FCSTD DOCUMENT  (FreeCAD 0.21R33771 (Git))
Label: bridge
License: All rights reserved
objects: Part::FeaturePython×22, Part::Mirroring×11, Part::MultiFuse×7, App::FeaturePython×7, Sketcher::SketchObject×5, Part::Extrusion×4, Part::Sweep×3, App::Part×3, Part::Compound×2, Part::Loft×1, Spreadsheet::Sheet×1
note: 54 computed .brp shape members not serialized (recipe doc carries the construction recipe); baked Part::Feature solids carry a one-line shape summary decoded from their .brp

FEATURE [Sketcher::SketchObject] Sketch
  FullyConstrained = true
  sketch-geometry (5):
    g0: LineSegment StartX=-680 StartY=-750 StartZ=0 EndX=-680 EndY=750 EndZ=0
    g1: LineSegment StartX=-680 StartY=750 StartZ=0 EndX=680 EndY=750 EndZ=0
    g2: LineSegment StartX=680 StartY=750 StartZ=0 EndX=680 EndY=-750 EndZ=0
    g3: LineSegment StartX=680 StartY=-750 StartZ=0 EndX=-680 EndY=-750 EndZ=0
    g4: GeomPoint X=0 Y=0 Z=0
  constraints (12):
    c: Coincident(g0,g1)
    c: Coincident(g1,g2)
    c: Coincident(g2,g3)
    c: Coincident(g3,g0)
    c: Horizontal(g1)
    c: Horizontal(g3)
    c: Vertical(g0)
    c: Vertical(g2)
    c: Symmetric(g1,g0,g4)
    c: Coincident(g4,g-1)
    c: DistanceY(g2,g2) = 1500
    c: DistanceX(g1,g1) = 1360
FEATURE [Part::FeaturePython] HShapeSteel  # WARN: FeaturePython — macro-defined, semantics opaque (R4)
  B = 150
  H = 150
  L = 1000
  Placement = pos=(530,0,-150) rot=(0,0,1;0rad)
  Solid = false
  g0 = 7.85
  mass = 0
  size = 2
  standard = SS_Wide
  t1 = 7
  t2 = 10
FEATURE [Part::Sweep] Sweep
  Frenet = true
  Sections = -> [HShapeSteel]
  Solid = true
  Spine = -> Sketch [Edge3,Edge2,Edge1,Edge4]
  Transition = 1
FEATURE [Part::FeaturePython] HShapeSteel001  # WARN: FeaturePython — macro-defined, semantics opaque (R4)
  B = 150
  H = 150
  L = 1000
  Placement = pos=(607.98,425,-75) rot=(0.57735,0.57735,0.57735;2.0944rad)
  Solid = true
  g0 = 7.85
  mass = 31.5089
  size = 2
  standard = SS_Wide
  t1 = 7
  t2 = 10
FEATURE [Part::FeaturePython] Clone  label="HShapeSteel002"  # Draft clone (typed FeaturePython)
  AttacherType = Attacher::AttachEngine3D
  Fuse = false
  Objects = -> [HShapeSteel001]
  Placement = pos=(607.98,-425,-75) rot=(0.57735,0.57735,0.57735;2.0944rad)
  Scale = (1,1,1)
FEATURE [Part::FeaturePython] HShapeSteel002  label="HShapeSteel003"  # WARN: FeaturePython — macro-defined, semantics opaque (R4)
  B = 150
  H = 150
  L = 1000
  Placement = pos=(1607.98,-500,-150) rot=(0,0,1;1.5708rad)
  Solid = false
  g0 = 7.85
  mass = 0
  size = 2
  standard = SS_Wide
  t1 = 7
  t2 = 10
FEATURE [Part::FeaturePython] HShapeSteel003  label="HShapeSteel004"  # WARN: FeaturePython — macro-defined, semantics opaque (R4)
  B = 150
  H = 194
  L = 1000
  Placement = pos=(1900,-500,-194) rot=(0,0,1;1.5708rad)
  Solid = false
  g0 = 7.85
  mass = 0
  size = 1
  standard = SS_Medium
  t1 = 6
  t2 = 9
FEATURE [Part::Loft] Loft
  Closed = false
  MaxDegree = 5
  Ruled = false
  Sections = -> [HShapeSteel002,HShapeSteel003]
  Solid = true
FEATURE [Part::Extrusion] Extrude
  Base = -> HShapeSteel003
  Dir = (-1,-2e-16,0)
  DirMode = 2
  FaceMakerClass = Part::FaceMakerBullseye
  LengthFwd = 6250
  LengthRev = 0
  Reversed = true
  Solid = true
  Symmetric = false
  expr: LengthFwd = Spreadsheet.L0
FEATURE [Part::MultiFuse] Fusion
  Shapes = -> [HShapeSteel001,Clone]
FEATURE [Part::MultiFuse] Fusion002
  Shapes = -> [Extrude,Loft]
FEATURE [Part::FeaturePython] Clone001  label="Fusion003"  # Draft clone (typed FeaturePython)
  AttacherType = Attacher::AttachEngine3D
  Fuse = false
  Objects = -> [Fusion002]
  Placement = pos=(-9.09e-13,850,6.6e-14) rot=(0,0,1;0rad)
  Scale = (1,1,1)
FEATURE [Part::Mirroring] Mirror  label="Fusion (mirrored)"
  Base = (0,0,0)
  Normal = (1,0,0)
  Source = -> Fusion
FEATURE [Part::MultiFuse] Fusion003  label="Fusion004"
  Refine = true
  Shapes = -> [Sweep,Fusion,Mirror]
FEATURE [Spreadsheet::Sheet] Spreadsheet
  cells = A2='tankdia   dia; B2(dia)=15500; A3='L0; B3(L0)==dia / 2 + 400 - 1900; A4='n; B4(n)==L0 / 700
FEATURE [Sketcher::SketchObject] Sketch001
  ExternalGeometry = -> [Fusion003]
  FullyConstrained = true
  sketch-geometry (4):
    g0: LineSegment StartX=-1150 StartY=-1150 StartZ=0 EndX=-1150 EndY=1150 EndZ=0
    g1: LineSegment StartX=-1150 StartY=1150 StartZ=0 EndX=1150 EndY=1150 EndZ=0
    g2: LineSegment StartX=1150 StartY=1150 StartZ=0 EndX=1150 EndY=-1150 EndZ=0
    g3: LineSegment StartX=-1150 StartY=-1150 StartZ=0 EndX=1150 EndY=-1150 EndZ=0
  constraints (12):
    c: Vertical(g0)
    c: Coincident(g0,g1)
    c: Horizontal(g1)
    c: Coincident(g1,g2)
    c: Vertical(g2)
    c: DistanceX(g1,g1) = 2300
    c: DistanceX(g-2,g1) = 1150
    c: Coincident(g3,g0)
    c: Coincident(g3,g2)
    c: Horizontal(g3)
    c: DistanceY(g2,g2) = 2300
    c: DistanceY(g-1,g1) = 1150
FEATURE [Part::FeaturePython] ChannelSteel  # WARN: FeaturePython — macro-defined, semantics opaque (R4)
  B = 75
  H = 150
  L = 1000
  Placement = pos=(-1150,855.871,-150) rot=(0,0,1;0rad)
  Solid = false
  g0 = 7.85
  mass = 0
  size = 3
  standard = SS
  t1 = 6.5
  t2 = 10
FEATURE [Part::Sweep] Sweep001
  Frenet = true
  Sections = -> [ChannelSteel]
  Solid = true
  Spine = -> Sketch001 [Edge2,Edge3,Edge4,Edge1]
  Transition = 1
FEATURE [Part::MultiFuse] Fusion004  label="Fusion005"
  Refine = true
  Shapes = -> [Fusion003,Sweep001]
FEATURE [Part::FeaturePython] AngleSteel  # WARN: FeaturePython — macro-defined, semantics opaque (R4)
  A = 75
  B = 75
  L = 700
  Placement = pos=(1800,350,-37.5) rot=(1,0,0;1.5708rad)
  Solid = true
  g0 = 7.85
  mass = 4.79514
  size = 10
  standard = SS_Equal
  t = 6
FEATURE [Part::FeaturePython] Array  # Draft array (typed FeaturePython)
  AlwaysSyncPlacement = false
  Angle = 360
  ArrayType = 0
  Axis = (0,0,1)
  Base = -> AngleSteel
  Center = (0,0,0)
  Count = 9
  ExpandArray = false
  Fuse = false
  IntervalAxis = (0,0,0)
  IntervalX = (700,0,0)
  IntervalY = (0,100,0)
  IntervalZ = (0,0,100)
  NumberCircles = 3
  NumberPolar = 5
  NumberX = 9
  NumberY = 1
  NumberZ = 1
  PlacementList = 9 placements: arithmetic series from (1800,350,-37.5) step (700,0,0) to (7400,350,-37.5)
  RadialDistance = 50
  ScaleList = (9) [(1,1,1),(1,1,1),(1,1,1),(1,1,1),(1,1,1),(1,1,1),(1,1,1),(1,1,1),(1,1,1)]
  Symmetry = 1
  TangentialDistance = 25
  expr: NumberX = Spreadsheet.n
FEATURE [Part::Compound] Compound
  Links = -> [Fusion002,Clone001]
FEATURE [Part::Compound] Compound001
  Links = -> [Compound,Array]
FEATURE [Part::FeaturePython] AngleSteel001  # WARN: FeaturePython — macro-defined, semantics opaque (R4)
  A = 75
  B = 75
  L = 325
  Placement = pos=(-642.5,-750,-37.5) rot=(1,0,0;1.5708rad)
  Solid = true
  g0 = 7.85
  mass = 2.22632
  size = 10
  standard = SS_Equal
  t = 6
FEATURE [Part::Mirroring] Mirror001  label="AngleSteel001 (mirrored)"
  Base = (0,0,0)
  Normal = (-1,0,0)
  Source = -> AngleSteel001
FEATURE [Part::Mirroring] Mirror002  label="AngleSteel001 (mirrored)001"
  Base = (0,0,0)
  Normal = (0,1,0)
  Source = -> AngleSteel001
FEATURE [Part::Mirroring] Mirror003  label="AngleSteel001 (mirrored) (mirrored)"
  Base = (0,0,0)
  Normal = (0,1,0)
  Source = -> Mirror001
FEATURE [Part::FeaturePython] HShapeSteel004  label="HShapeSteel005"  # WARN: FeaturePython — macro-defined, semantics opaque (R4)
  B = 150
  H = 194
  L = 850
  Placement = pos=(8075,425,-97) rot=(1,0,0;1.5708rad)
  Solid = true
  g0 = 7.85
  mass = 26.0299
  size = 1
  standard = SS_Medium
  t1 = 6
  t2 = 9
FEATURE [Part::MultiFuse] Fusion005  label="Fusion006"
  Shapes = -> [Compound001]
FEATURE [Part::MultiFuse] Fusion006  label="Fusion007"
  Refine = true
  Shapes = -> [Fusion005,HShapeSteel004]
FEATURE [Part::Mirroring] Mirror004  label="Fusion007 (mirrored)"
  Base = (0,-500,0)
  Normal = (1,0,0)
  Source = -> Fusion006
FEATURE [Sketcher::SketchObject] Sketch002
  ExternalGeometry = -> [Sketch001,Fusion006,Fusion004]
  FullyConstrained = true
  MapMode = 5
  Placement = pos=(0,0,1.92e-13) rot=(0,0,1;0rad)
  Support = -> [Mirror004]
  sketch-geometry (12):
    g0: LineSegment StartX=0 StartY=1150 StartZ=0 EndX=1150 EndY=1150 EndZ=0
    g1: LineSegment StartX=1150 StartY=1150 StartZ=0 EndX=1150 EndY=500 EndZ=0
    g2: LineSegment StartX=1150 StartY=500 StartZ=0 EndX=8150 EndY=500 EndZ=0
    g3: LineSegment StartX=8150 StartY=500 StartZ=0 EndX=8150 EndY=-500 EndZ=0
    g4: LineSegment StartX=8150 StartY=-500 StartZ=0 EndX=1150 EndY=-500 EndZ=0
    g5: LineSegment StartX=1150 StartY=-500 StartZ=0 EndX=1150 EndY=-1150 EndZ=0
    g6: LineSegment StartX=1150 StartY=-1150 StartZ=0 EndX=0 EndY=-1150 EndZ=0
    g7: LineSegment StartX=0 StartY=-1150 StartZ=0 EndX=0 EndY=-675 EndZ=0
    g8: LineSegment StartX=0 StartY=675 StartZ=0 EndX=605 EndY=675 EndZ=0
    g9: LineSegment StartX=605 StartY=675 StartZ=0 EndX=605 EndY=-675 EndZ=0
    g10: LineSegment StartX=605 StartY=-675 StartZ=0 EndX=0 EndY=-675 EndZ=0
    g11: LineSegment StartX=0 StartY=675 StartZ=0 EndX=0 EndY=1150 EndZ=0
  constraints (32):
    c: Horizontal(g0)
    c: Coincident(g0,g1)
    c: Vertical(g1)
    c: Coincident(g1,g2)
    c: Horizontal(g2)
    c: Coincident(g2,g3)
    c: Coincident(g3,g4)
    c: Horizontal(g4)
    c: Coincident(g4,g5)
    c: Coincident(g5,g6)
    c: PointOnObject(g6,g-2)
    c: Horizontal(g6)
    c: Coincident(g6,g7)
    c: Coincident(g11,g0)
    c: Vertical(g7)
    c: Coincident(g-3,g0)
    c: Coincident(g5,g-3)
    c: Coincident(g3,g-4)
    c: Coincident(g2,g-4)
    c: Vertical(g5)
    c: Horizontal(g8)
    c: Coincident(g8,g9)
    c: Vertical(g9)
    c: Coincident(g9,g10)
    c: Horizontal(g10)
    c: Coincident(g7,g10)
    c: Coincident(g11,g8)
    c: Distance(g8,g-5) = 75
    c: Distance(g7,g-6) = 75
    c: DistanceX(g-6,g9) = 75
    c: PointOnObject(g8,g-2)
    c: Vertical(g11)
FEATURE [Part::Extrusion] Extrude001
  Base = -> Sketch002
  Dir = (0,-1e-16,1)
  DirMode = 2
  FaceMakerClass = Part::FaceMakerBullseye
  LengthFwd = 4.5
  LengthRev = 0
  Solid = true
  Symmetric = false
FEATURE [Part::Mirroring] Mirror005  label="Extrude001 (mirrored)"
  Base = (0,2000,0)
  Normal = (1,0,0)
  Source = -> Extrude001
FEATURE [Part::FeaturePython] Channel  label="handrail"  # WARN: FeaturePython — macro-defined, semantics opaque (R4)
  Placement = pos=(0,-1124.19,0) rot=(0,0,1;0rad)
  Reverse = false
  g0 = 7.85
  h = 1100
  k = 90
  l1 = 1125
  l2 = 300
  mass = 31.5207
  p = 1000
  spec = 0
  type = 6
FEATURE [Part::FeaturePython] handrail_001  # a2plus imported part (geometry in sourceFile) (typed FeaturePython)
  Placement = pos=(0,-0.68,0) rot=(0,0,1;0rad)
  a2p_Version = 0.4.60n
  fixedPosition = true
  localSourceObject = Channel
  objectType = a2pPart
  sourceFile = converted
  subassemblyImport = false
  timeLastImport = 1.7091e+09
  updateColors = true
FEATURE [App::FeaturePython] circularEdge_001_mirror  label="circularEdge_001__handrail_001"  # a2plus constraint (typed FeaturePython)
  Object1 = handrail_001
  Object2 = Corner
  SubElement1 = Edge96
  SubElement2 = Edge44
  Suppressed = false
  Type = circularEdge
  directionConstraint = 0
  lockRotation = false
  offset = 0
FEATURE [Part::Mirroring] Mirror006  label="handrail_001 (mirrored)"
  Base = (0,0,4.5)
  Normal = (0,-1,0)
  Source = -> handrail_001
FEATURE [Part::FeaturePython] BasePlate  # WARN: FeaturePython — macro-defined, semantics opaque (R4)
  B = 150
  D = 20
  H = 150
  b1 = 30
  h1 = 45
  sface = 0
FEATURE [Part::Extrusion] Extrude002
  Base = -> BasePlate
  Dir = (0,0,1)
  DirMode = 2
  FaceMakerClass = Part::FaceMakerBullseye
  LengthFwd = 10
  LengthRev = 0
  Solid = true
  Symmetric = false
FEATURE [Part::FeaturePython] H_Shape  # WARN: FeaturePython — macro-defined, semantics opaque (R4)
  B = 150
  H = 150
  L = 100
  Solid = true
  g0 = 7.85
  mass = 3.15089
  size = 2
  standard = SS_Wide
FEATURE [Part::MultiFuse] Fusion007  label="PostH"
  Placement = pos=(-8074.83,-425.97,-294.128) rot=(0,0,1;1.5708rad)
  Shapes = -> [Extrude002,H_Shape]
FEATURE [Part::Mirroring] Mirror008  label="PostH (mirrored)"
  Base = (-8000,1.2506e-12,1.563e-13)
  Normal = (-4e-16,1,0)
  Source = -> Fusion007
FEATURE [Part::Mirroring] Mirror009  label="PostH (mirrored) (mirrored)"
  Base = (0,-400,0)
  Normal = (1,0,0)
  Source = -> Mirror008
FEATURE [Part::Mirroring] Mirror010  label="PostH (mirrored)001"
  Base = (0,-400,0)
  Normal = (1,0,0)
  Source = -> Fusion007
FEATURE [Sketcher::SketchObject] Sketch003
  ExternalGeometry = -> [Fusion006]
  FullyConstrained = false
  MapMode = 5
  Placement = pos=(0,0,1.92e-13) rot=(0,0,1;0rad)
  Support = -> [Fusion006]
  sketch-geometry (3):
    g0: LineSegment StartX=8150 StartY=-428 StartZ=0 EndX=8150 EndY=-878 EndZ=0
    g1: LineSegment StartX=8150 StartY=-878 StartZ=0 EndX=6692.47 EndY=-878 EndZ=0
    g2: LineSegment StartX=6692.47 StartY=-878 StartZ=0 EndX=6692.47 EndY=-428 EndZ=0
  constraints (8):
    c: Vertical(g0)
    c: Coincident(g0,g1)
    c: Horizontal(g1)
    c: Coincident(g1,g2)
    c: Vertical(g2)
    c: Coincident(g0,g-3)
    c: DistanceY(g0,g0) = 450
    c: PointOnObject(g2,g-3)
FEATURE [Part::FeaturePython] ChannelSteel001  # WARN: FeaturePython — macro-defined, semantics opaque (R4)
  B = 75
  H = 150
  L = 1000
  Placement = pos=(6767.42,-671.206,-150) rot=(0,0,1;3.14159rad)
  Solid = false
  g0 = 7.85
  mass = 0
  size = 3
  standard = SS
  t1 = 6.5
  t2 = 10
FEATURE [Part::Sweep] Sweep002
  Frenet = false
  Sections = -> [ChannelSteel001]
  Solid = true
  Spine = -> Sketch003 [Edge3,Edge2,Edge1]
  Transition = 1
FEATURE [Sketcher::SketchObject] Sketch004
  ExternalGeometry = -> [Sketch003,Extrude001]
  FullyConstrained = true
  MapMode = 5
  Placement = pos=(0,0,9.3e-14) rot=(0,0,1;0rad)
  Support = -> [Sweep002]
  sketch-geometry (4):
    g0: LineSegment StartX=6692.47 StartY=-878 StartZ=0 EndX=8150 EndY=-878 EndZ=0
    g1: LineSegment StartX=8150 StartY=-878 StartZ=0 EndX=8150 EndY=-500 EndZ=0
    g2: LineSegment StartX=8150 StartY=-500 StartZ=0 EndX=6692.47 EndY=-500 EndZ=0
    g3: LineSegment StartX=6692.47 StartY=-500 StartZ=0 EndX=6692.47 EndY=-878 EndZ=0
  constraints (10):
    c: Coincident(g0,g1)
    c: Coincident(g1,g2)
    c: Coincident(g2,g3)
    c: Coincident(g3,g0)
    c: Horizontal(g0)
    c: Horizontal(g2)
    c: Vertical(g1)
    c: Vertical(g3)
    c: Coincident(g1,g-4)
    c: Coincident(g0,g-5)
FEATURE [Part::Extrusion] Extrude003
  Base = -> Sketch004
  Dir = (0,-1e-16,1)
  DirMode = 2
  FaceMakerClass = Part::FaceMakerBullseye
  LengthFwd = 4.5
  LengthRev = 0
  Solid = true
  Symmetric = false
FEATURE [App::Part] Part  label="bridge001"
  Group = -> [Sketch002,HShapeSteel,HShapeSteel001,ChannelSteel,AngleSteel,Mirror,Mirror004,Compound,Compound001,Array,Extrude,Extrude001,HShapeSteel002,Clone,Clone001,HShapeSteel003,HShapeSteel004,Loft,Fusion006,Sweep001,Sweep,Fusion003,Fusion004,Fusion002,Fusion005,Fusion,Sketch,Sketch001,Mirror005,Mirror001,Mirror002,AngleSteel001,Mirror003,Extrude002,BasePlate,H_Shape,Fusion007,Mirror008,Mirror010,+6 more]
  Origin = -> Origin
FEATURE [Part::FeaturePython] Channel001  # WARN: FeaturePython — macro-defined, semantics opaque (R4)
  Placement = pos=(7421,-850.87,-2.274e-13) rot=(0,0,1;0rad)
  Reverse = false
  g0 = 7.85
  h = 1100
  k = 90
  l1 = 700
  l2 = 200
  mass = 20.0308
  p = 1000
  spec = 0
  type = 6
FEATURE [Part::FeaturePython] Corner001  # WARN: FeaturePython — macro-defined, semantics opaque (R4)
  Placement = pos=(6325,-474.87,-2.274e-13) rot=(0,0,1;0rad)
  Reverse = false
  g0 = 7.85
  h = 1100
  k = -90
  l1 = 396
  l2 = 176
  mass = 4.57145
  p = 1000
  spec = 0
  type = 2
FEATURE [Part::FeaturePython] Compound003_001  # a2plus imported part (geometry in sourceFile) (typed FeaturePython)
  a2p_Version = 0.4.60n
  fixedPosition = true
  localSourceObject = Compound003
  objectType = a2pPart
  sourceFile = converted
  subassemblyImport = false
  timeLastImport = 1.70947e+09
  updateColors = true
FEATURE [App::FeaturePython] circularEdge_002  label="circularEdge_002__Corner001"  # a2plus constraint (typed FeaturePython)
  Object1 = Compound003_001
  Object2 = Corner001
  ParentTreeObject = -> Compound003_001
  SubElement1 = Edge689
  SubElement2 = Edge10
  Suppressed = false
  Type = circularEdge
  directionConstraint = 0
  lockRotation = false
  offset = 0
FEATURE [App::FeaturePython] circularEdge_002_mirror  label="circularEdge_002__Compound003_001"  # a2plus constraint (typed FeaturePython)
  Object1 = Compound003_001
  Object2 = Corner001
  ParentTreeObject = -> Corner001
  SubElement1 = Edge689
  SubElement2 = Edge10
  Suppressed = false
  Type = circularEdge
  directionConstraint = 0
  lockRotation = false
  offset = 0
FEATURE [App::FeaturePython] circularEdge_003  label="circularEdge_003__Channel001"  # a2plus constraint (typed FeaturePython)
  Object1 = Corner001
  Object2 = Channel001
  ParentTreeObject = -> Corner001
  SubElement1 = Edge2
  SubElement2 = Edge93
  Suppressed = false
  Type = circularEdge
  directionConstraint = 0
  lockRotation = false
  offset = 0
FEATURE [App::FeaturePython] circularEdge_003_mirror  label="circularEdge_003__Corner001"  # a2plus constraint (typed FeaturePython)
  Object1 = Corner001
  Object2 = Channel001
  ParentTreeObject = -> Channel001
  SubElement1 = Edge2
  SubElement2 = Edge93
  Suppressed = false
  Type = circularEdge
  directionConstraint = 0
  lockRotation = false
  offset = 0
FEATURE [Part::FeaturePython] StraightLine  # WARN: FeaturePython — macro-defined, semantics opaque (R4)
  Placement = pos=(6325,474.87,-2.274e-13) rot=(0,0,1;0rad)
  Reverse = false
  g0 = 7.85
  h = 1100
  l1 = 1800
  mass = 27.8373
  p = 500
  spec = 0
  type = 0
FEATURE [Part::FeaturePython] Corner  # WARN: FeaturePython — macro-defined, semantics opaque (R4)
  Placement = pos=(-1125,824.87,-1.137e-13) rot=(0,0,1;4.71239rad)
  Reverse = false
  g0 = 7.85
  h = 1100
  k = -90
  l1 = 350
  l2 = 7000
  mass = 100.741
  p = 500
  spec = 0
  type = 2
FEATURE [Part::FeaturePython] handrail_001__mirrored__001  label="handrail_001 (mirrored)_001"  # a2plus imported part (geometry in sourceFile) (typed FeaturePython)
  a2p_Version = 0.4.60n
  fixedPosition = true
  localSourceObject = Mirror006
  objectType = a2pPart
  sourceFile = converted
  subassemblyImport = false
  timeLastImport = 1.70947e+09
  updateColors = true
FEATURE [App::FeaturePython] circularEdge_001  label="circularEdge_001__Corner"  # a2plus constraint (typed FeaturePython)
  Object1 = handrail_001__mirrored__001
  Object2 = Corner
  ParentTreeObject = -> handrail_001__mirrored__001
  SubElement1 = Edge107
  SubElement2 = Edge17
  Suppressed = false
  Type = circularEdge
  directionConstraint = 0
  lockRotation = false
  offset = 0
FEATURE [App::FeaturePython] circularEdge_001_mirror001  label="circularEdge_001__handrail_001 (mirrored)_001"  # a2plus constraint (typed FeaturePython)
  Object1 = handrail_001__mirrored__001
  Object2 = Corner
  ParentTreeObject = -> Corner
  SubElement1 = Edge107
  SubElement2 = Edge17
  Suppressed = false
  Type = circularEdge
  directionConstraint = 0
  lockRotation = false
  offset = 0
FEATURE [Part::Mirroring] Mirror011  label="Corner (mirrored)"
  Base = (0,0,0)
  Normal = (0,1,0)
  Source = -> Corner
FEATURE [App::Part] Part001  label="handrail001"
  Group = -> [Channel,handrail_001,circularEdge_001_mirror,Mirror006,Channel001,Corner001,Compound003_001,StraightLine,Corner,circularEdge_003,circularEdge_002_mirror,circularEdge_003_mirror,handrail_001__mirrored__001,circularEdge_001_mirror001,Mirror011]
  Origin = -> Origin001
FEATURE [App::Part] Part002  label="bridge"
  Group = -> [Part001,Part,Spreadsheet]
  Origin = -> Origin002
